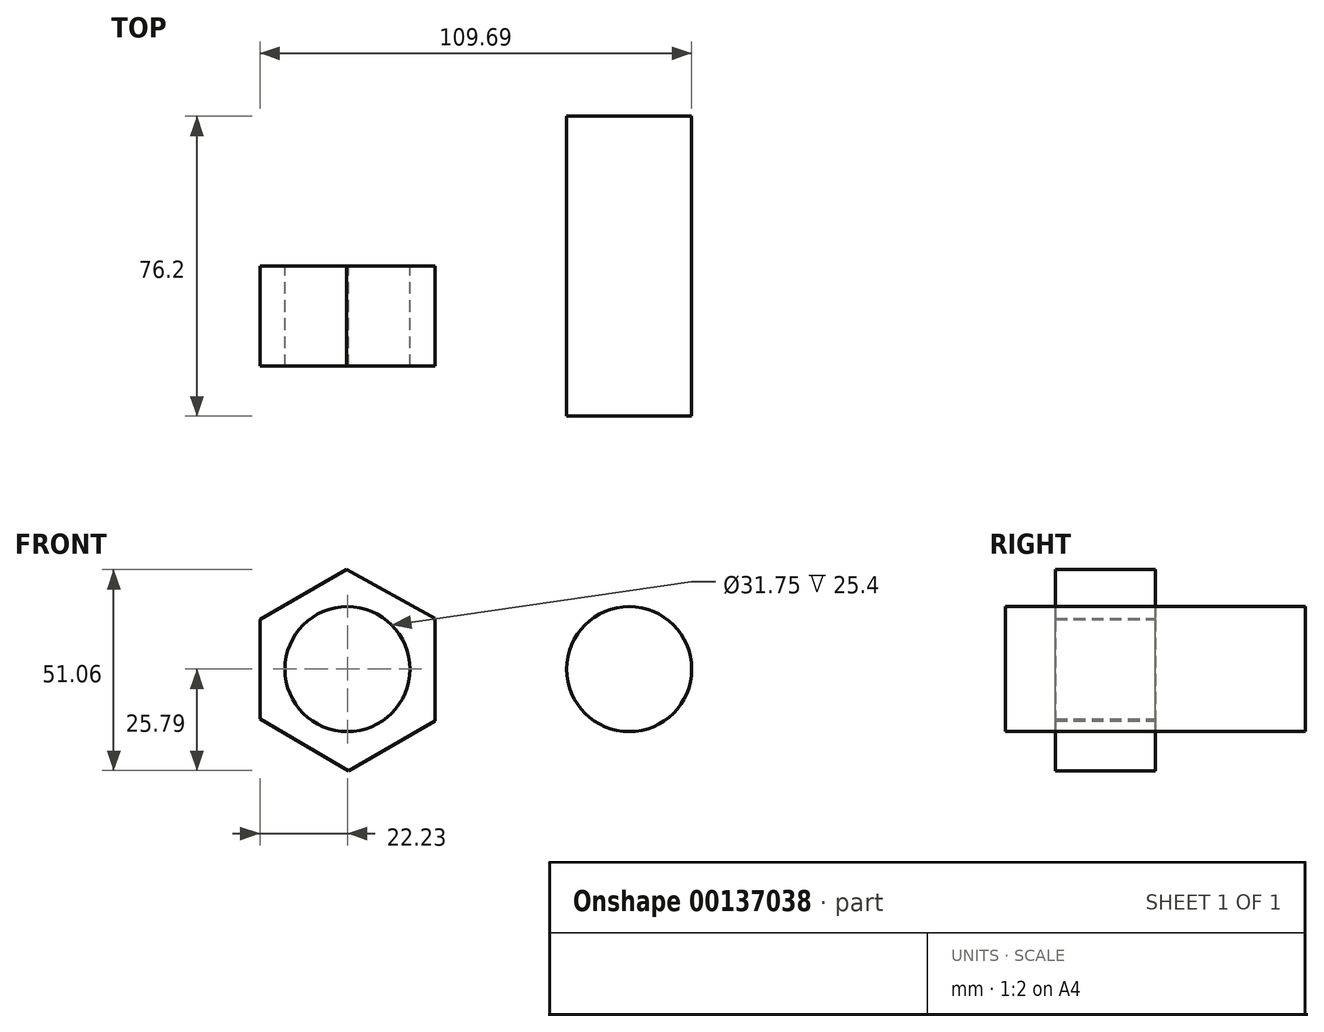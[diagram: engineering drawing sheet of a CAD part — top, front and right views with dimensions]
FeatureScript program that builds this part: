
annotation { "Feature Type Name" : "Feature", "Feature Type Description" : "" }
export const myFeature = defineFeature(function(context is Context, id is Id, definition is map)
    precondition{}
    {
        {
            var Q0;
            Q0=qCreatedBy(makeId("Front.planeOp"),FACE);
            var sketch = newSketch(context, id + "F0", { "sketchPlane" : qUnion([Q0])});
            skLineSegment(sketch, "E0", {"start": v(-22.23, 12.57) * mm, "end": v(-22.23, -12.7) * mm});
            skLineSegment(sketch, "E1", {"start": v(-22.23, -12.7) * mm, "end": v(0.23, -25.8) * mm});
            skLineSegment(sketch, "E2", {"start": v(0.23, -25.8) * mm, "end": v(22.23, -13.1) * mm});
            skLineSegment(sketch, "E3", {"start": v(22.22, -13.1) * mm, "end": v(22.22, 12.83) * mm});
            skLineSegment(sketch, "E4", {"start": v(22.22, 12.83) * mm, "end": v(-0.23, 25.27) * mm});
            skLineSegment(sketch, "E5", {"start": v(-0.23, 25.27) * mm, "end": v(-22.23, 12.57) * mm});
            skCircle(sketch, "E6", {"center": v(0, 0) * mm, "radius": 15.88 * mm});
            skCircle(sketch, "E7", {"center": v(71.59, 0) * mm, "radius": 15.88 * mm});
            skSolve(sketch);
        }
        {
            var Q0;
            Q0=makeQuery(id+"F0.imprint","IMPRINT",FACE,{"disambiguationData":[TD([[makeQuery(id+"F0.imprint","IMPRINT",EDGE,{"derivedFrom":sQuery(id+"F0.wireOp",EDGE,"E0")}),1.0]])]});
            extrude(context, id + "F1", {"entities" : qUnion([Q0]), "depth" : 25.4 * mm});
        }
        {
            var Q0;
            Q0=makeQuery(id+"F0.imprint","IMPRINT",FACE,{"disambiguationData":[TD([[makeQuery(id+"F0.imprint","IMPRINT",EDGE,{"derivedFrom":sQuery(id+"F0.wireOp",EDGE,"E7")}),1.0]])]});
            extrude(context, id + "F2", {"entities" : qUnion([Q0]), "endBound" : BoundingType.SYMMETRIC, "depth" : 76.2 * mm});
        }
    });
